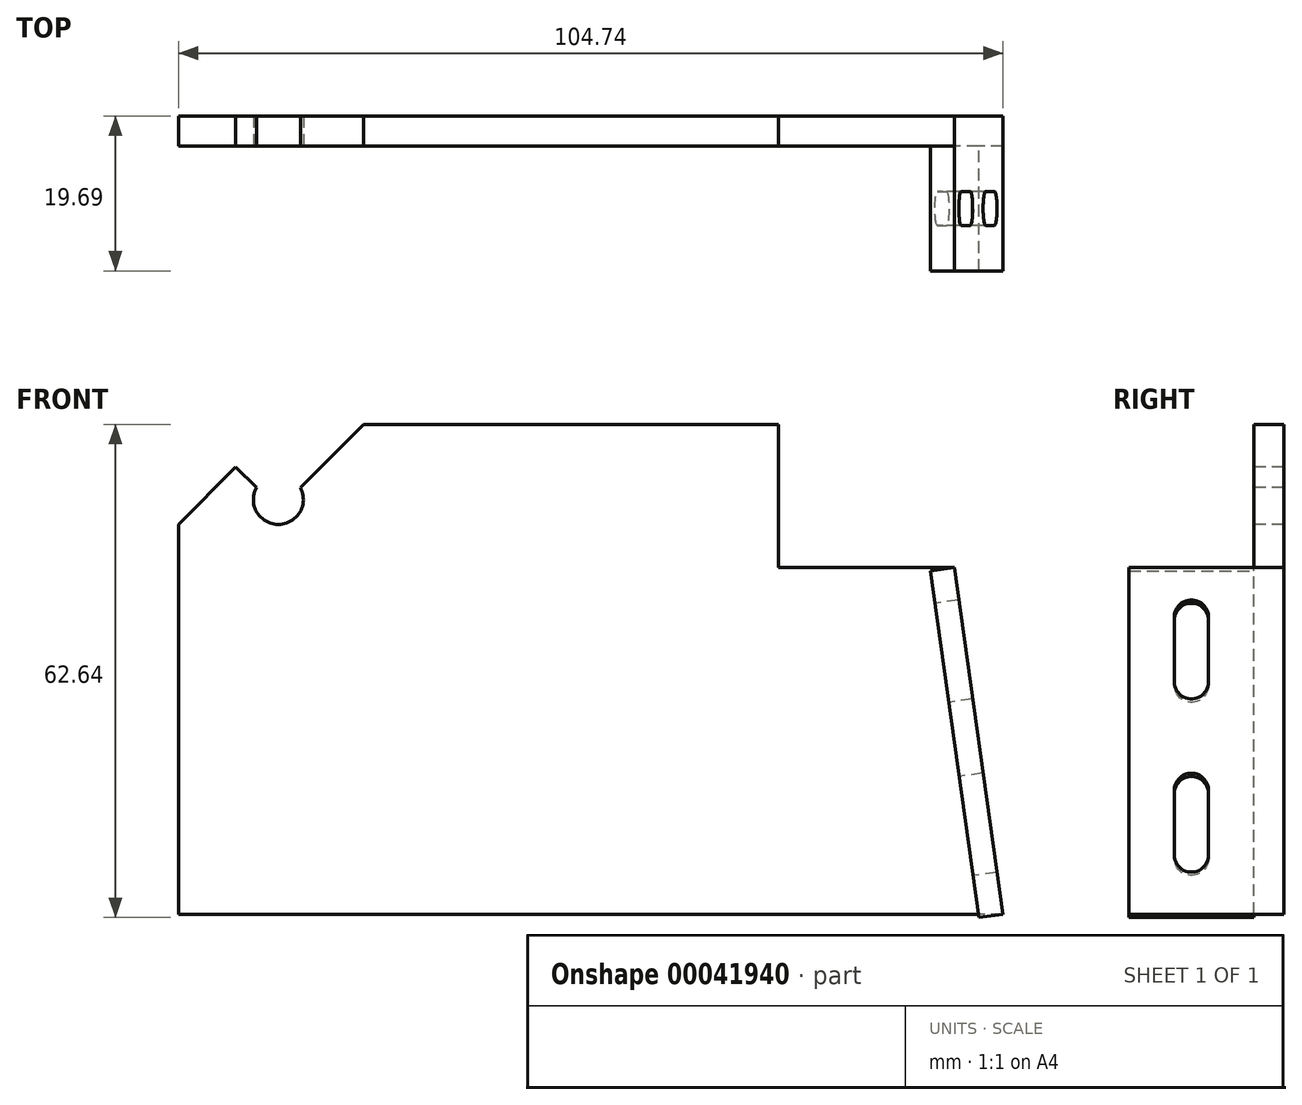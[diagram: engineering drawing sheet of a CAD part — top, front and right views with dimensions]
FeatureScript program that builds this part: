
annotation { "Feature Type Name" : "Feature", "Feature Type Description" : "" }
export const myFeature = defineFeature(function(context is Context, id is Id, definition is map)
    precondition{}
    {
        {
            var Q0;
            Q0=qCreatedBy(makeId("Front.planeOp"),FACE);
            var sketch = newSketch(context, id + "F0", { "sketchPlane" : qUnion([Q0])});
            skLineSegment(sketch, "E0", {"start": v(3.02, -43.6) * mm, "end": v(9.2, -87.62) * mm});
            skLineSegment(sketch, "E1", {"start": v(9.2, -87.62) * mm, "end": v(6.19, -88.04) * mm});
            skLineSegment(sketch, "E2", {"start": v(6.19, -88.04) * mm, "end": v(0, -44.02) * mm});
            skLineSegment(sketch, "E3", {"start": v(0, -44.02) * mm, "end": v(3.02, -43.6) * mm});
            skLineSegment(sketch, "E4", {"start": v(0, 0) * mm, "end": v(43.58, 0) * mm, "construction": true});
            skPoint(sketch, "E5", {"position": v(4.48, -53.98) * mm});
            skPoint(sketch, "E6", {"position": v(7.57, -75.98) * mm});
            skSolve(sketch);
        }
        {
            var Q0;
            Q0 = qSketchRegion(id + "F0", true);
            extrude(context, id + "F1", {"entities" : qUnion([Q0]), "depth" : 15.88 * mm});
        }
        {
            var Q0;
            Q0=makeQuery(id+"F1.opExtrude","SWEPT_FACE",FACE,{"disambiguationData":[OSD([sQuery(id+"F0.wireOp",EDGE,"E2")])]});
            var sketch = newSketch(context, id + "F2", { "sketchPlane" : qUnion([Q0])});
            skLineSegment(sketch, "E7.bottom", {"start": v(5.78, -47.72) * mm, "end": v(10.1, -47.72) * mm});
            skLineSegment(sketch, "E7.top", {"start": v(5.78, -60.42) * mm, "end": v(10.1, -60.42) * mm});
            skLineSegment(sketch, "E7.left", {"start": v(5.78, -47.72) * mm, "end": v(5.78, -60.42) * mm});
            skLineSegment(sketch, "E7.right", {"start": v(10.1, -47.72) * mm, "end": v(10.1, -60.42) * mm});
            skLineSegment(sketch, "E8.bottom", {"start": v(5.78, -69.95) * mm, "end": v(10.1, -69.95) * mm});
            skLineSegment(sketch, "E8.top", {"start": v(5.78, -82.65) * mm, "end": v(10.1, -82.65) * mm});
            skLineSegment(sketch, "E8.left", {"start": v(5.78, -69.95) * mm, "end": v(5.78, -82.65) * mm});
            skLineSegment(sketch, "E8.right", {"start": v(10.1, -69.95) * mm, "end": v(10.1, -82.65) * mm});
            skPoint(sketch, "E9", {"position": v(10.1, -54.07) * mm});
            skLineSegment(sketch, "E10", {"start": v(7.94, -43.6) * mm, "end": v(7.94, -47.72) * mm, "construction": true});
            skSolve(sketch);
        }
        {
            var Q0;
            Q0 = qSketchRegion(id + "F2", true);
            extrude(context, id + "F3", {"entities" : qUnion([Q0]), "operationType" : NewBodyOperationType.REMOVE, "endBound" : BoundingType.THROUGH_ALL, "oppositeDirection" : true, "depth" : 25.4 * mm});
        }
        {
            var Q0;
            Q0=makeQuery(id+"F3.boolean.opBoolean","COPY",EDGE,{"derivedFrom":makeQuery(id+"F3.opExtrude","SWEPT_EDGE",EDGE,{"disambiguationData":[OSD([sQuery(id+"F2.wireOp",EDGE,"E7.bottom"),sQuery(id+"F2.wireOp",EDGE,"E7.left")])]})});
            var Q1;
            Q1=makeQuery(id+"F3.boolean.opBoolean","COPY",EDGE,{"derivedFrom":makeQuery(id+"F3.opExtrude","SWEPT_EDGE",EDGE,{"disambiguationData":[OSD([sQuery(id+"F2.wireOp",EDGE,"E8.bottom"),sQuery(id+"F2.wireOp",EDGE,"E8.left")])]})});
            var Q2;
            Q2=makeQuery(id+"F3.boolean.opBoolean","COPY",EDGE,{"derivedFrom":makeQuery(id+"F3.opExtrude","SWEPT_EDGE",EDGE,{"disambiguationData":[OSD([sQuery(id+"F2.wireOp",EDGE,"E8.bottom"),sQuery(id+"F2.wireOp",EDGE,"E8.right")])]})});
            var Q3;
            Q3=makeQuery(id+"F3.boolean.opBoolean","COPY",EDGE,{"derivedFrom":makeQuery(id+"F3.opExtrude","SWEPT_EDGE",EDGE,{"disambiguationData":[OSD([sQuery(id+"F2.wireOp",EDGE,"E7.bottom"),sQuery(id+"F2.wireOp",EDGE,"E7.right")])]})});
            var Q4;
            Q4=makeQuery(id+"F3.boolean.opBoolean","COPY",EDGE,{"derivedFrom":makeQuery(id+"F3.opExtrude","SWEPT_EDGE",EDGE,{"disambiguationData":[OSD([sQuery(id+"F2.wireOp",EDGE,"E7.top"),sQuery(id+"F2.wireOp",EDGE,"E7.right")])]})});
            var Q5;
            Q5=makeQuery(id+"F3.boolean.opBoolean","COPY",EDGE,{"derivedFrom":makeQuery(id+"F3.opExtrude","SWEPT_EDGE",EDGE,{"disambiguationData":[OSD([sQuery(id+"F2.wireOp",EDGE,"E8.top"),sQuery(id+"F2.wireOp",EDGE,"E8.right")])]})});
            var Q6;
            Q6=makeQuery(id+"F3.boolean.opBoolean","COPY",EDGE,{"derivedFrom":makeQuery(id+"F3.opExtrude","SWEPT_EDGE",EDGE,{"disambiguationData":[OSD([sQuery(id+"F2.wireOp",EDGE,"E8.top"),sQuery(id+"F2.wireOp",EDGE,"E8.left")])]})});
            var Q7;
            Q7=makeQuery(id+"F3.boolean.opBoolean","COPY",EDGE,{"derivedFrom":makeQuery(id+"F3.opExtrude","SWEPT_EDGE",EDGE,{"disambiguationData":[OSD([sQuery(id+"F2.wireOp",EDGE,"E7.top"),sQuery(id+"F2.wireOp",EDGE,"E7.left")])]})});
            fillet(context, id + "F4", {"entities" : qUnion([Q0, Q1, Q2, Q3, Q4, Q5, Q6, Q7]), "radius" : 2.16 * mm, "tangentPropagation" : true, "allowEdgeOverflow" : false});
        }
        {
            var Q0;
            Q0=qCreatedBy(makeId("Front.planeOp"),FACE);
            var sketch = newSketch(context, id + "F5", { "sketchPlane" : qUnion([Q0])});
            skLineSegment(sketch, "E11", {"start": v(3.02, -43.6) * mm, "end": v(9.2, -87.62) * mm});
            skLineSegment(sketch, "E12", {"start": v(9.2, -87.62) * mm, "end": v(-95.54, -87.62) * mm});
            skLineSegment(sketch, "E13", {"start": v(-95.54, -87.62) * mm, "end": v(-95.54, -25.4) * mm});
            skLineSegment(sketch, "E14", {"start": v(-95.54, -25.4) * mm, "end": v(-19.34, -25.4) * mm});
            skLineSegment(sketch, "E15", {"start": v(-19.34, -25.4) * mm, "end": v(-19.34, -43.6) * mm});
            skLineSegment(sketch, "E16", {"start": v(-19.34, -43.6) * mm, "end": v(3.02, -43.6) * mm});
            skCircle(sketch, "E17", {"center": v(-82.84, -34.93) * mm, "radius": 3.18 * mm});
            skSolve(sketch);
        }
        {
            var Q0;
            Q0 = qSketchRegion(id + "F5", true);
            extrude(context, id + "F6", {"entities" : qUnion([Q0]), "operationType" : NewBodyOperationType.ADD, "oppositeDirection" : true, "depth" : 3.8 * mm});
        }
        {
            var Q0;
            Q0=qCreatedBy(makeId("Front.planeOp"),FACE);
            var sketch = newSketch(context, id + "F7", { "sketchPlane" : qUnion([Q0])});
            skLineSegment(sketch, "E18", {"start": v(-95.54, -38.1) * mm, "end": v(-82.84, -25.4) * mm});
            skLineSegment(sketch, "E19", {"start": v(-82.84, -25.4) * mm, "end": v(-95.54, -25.4) * mm});
            skLineSegment(sketch, "E20", {"start": v(-95.54, -25.4) * mm, "end": v(-95.54, -38.1) * mm});
            skSolve(sketch);
        }
        {
            var Q0;
            Q0 = qSketchRegion(id + "F7", true);
            extrude(context, id + "F8", {"entities" : qUnion([Q0]), "operationType" : NewBodyOperationType.REMOVE, "oppositeDirection" : true, "depth" : 25.4 * mm});
        }
        {
            var Q0;
            Q0=qCreatedBy(makeId("Front.planeOp"),FACE);
            var sketch = newSketch(context, id + "F9", { "sketchPlane" : qUnion([Q0])});
            skLineSegment(sketch, "E21", {"start": v(-82.84, -36.21) * mm, "end": v(-93.65, -25.4) * mm});
            skLineSegment(sketch, "E22", {"start": v(-93.65, -25.4) * mm, "end": v(-70.14, -25.4) * mm});
            skLineSegment(sketch, "E23", {"start": v(-70.14, -23.51) * mm, "end": v(-70.14, -25.4) * mm});
            skLineSegment(sketch, "E24", {"start": v(-70.14, -23.51) * mm, "end": v(-82.84, -36.21) * mm});
            skLineSegment(sketch, "E25", {"start": v(-85.63, -33.42) * mm, "end": v(-80.04, -33.42) * mm, "construction": true});
            skSolve(sketch);
        }
        {
            var Q0;
            Q0 = qSketchRegion(id + "F9", true);
            extrude(context, id + "F10", {"entities" : qUnion([Q0]), "operationType" : NewBodyOperationType.REMOVE, "oppositeDirection" : true, "depth" : 25.4 * mm});
        }
    });
